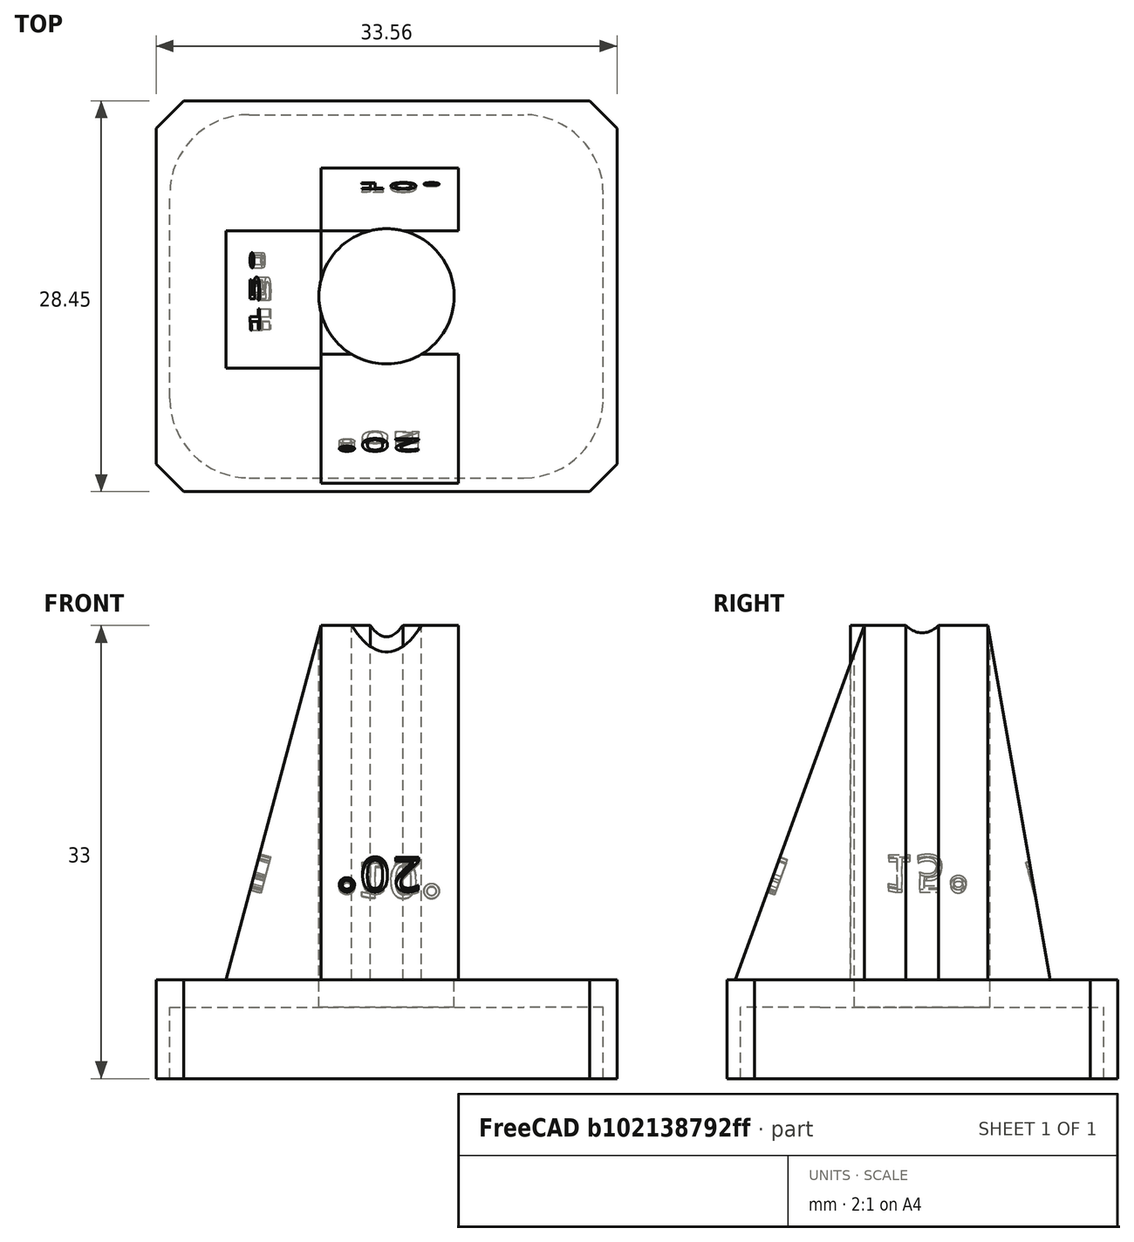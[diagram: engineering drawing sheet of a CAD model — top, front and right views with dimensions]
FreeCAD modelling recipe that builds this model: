
FCSTD DOCUMENT  (FreeCAD 0.19R24276 (Git))
Label: GuiaAfiladoTxeira
License: All rights reserved
LicenseURL: http://en.wikipedia.org/wiki/All_rights_reserved
objects: TechDraw::DrawViewDimension×12, TechDraw::DrawProjGroupItem×4, Part::Feature×3, Part::Box×2, Part::MultiFuse×2, TechDraw::DrawSVGTemplate×2, TechDraw::DrawViewPart×2, TechDraw::DrawPage×2, Part::Fillet×1, Part::Cylinder×1, Part::Offset×1, Part::Cut×1, Part::Chamfer×1, TechDraw::DrawProjGroup×1, TechDraw::DrawViewAnnotation×1
note: 12 computed .brp shape members not serialized (recipe doc carries the construction recipe); baked Part::Feature solids carry a one-line shape summary decoded from their .brp

FEATURE [Part::Box] Box  label="Cube"
  AttacherType = Attacher::AttachEngine3D
  Height = 5.2
  Length = 31.56
  Width = 26.45
FEATURE [Part::Fillet] Fillet
  Base = -> Box
  Edges = 4 edges r=5.78: [Edge1,Edge3,Edge5,Edge7]
FEATURE [Part::Box] Box001  label="Cube001"
  AttacherType = Attacher::AttachEngine3D
  Height = 7.2
  Length = 33.56
  Placement = pos=(-1,-1,0) rot=(0,0,1;0rad)
  Width = 28.45
FEATURE [Part::Cylinder] Cylinder
  Angle = 360
  AttacherType = Attacher::AttachEngine3D
  Height = 200
  Placement = pos=(15.78,13.22,0) rot=(0,0,1;0rad)
  Radius = 4.825
FEATURE [Part::Offset] Offset
  Fill = false
  Intersection = false
  Join = 0
  Mode = 0
  SelfIntersection = false
  Source = -> Cylinder
  Value = 0.1
FEATURE [Part::Feature] Part__Feature  label="Cut005"
  Placement = pos=(21,18,-5) rot=(0,-1,0;1.5708rad)
  shape: bbox 10 x 4.585 x 26 mm, 55 faces (baked)
FEATURE [Part::Feature] Part__Feature001  label="Cut006"
  Placement = pos=(11,9,-5) rot=(0.707107,0,0.707107;3.14159rad)
  shape: bbox 10 x 9.463 x 26 mm, 65 faces (baked)
FEATURE [Part::Feature] Part__Feature002  label="Cut001"
  Placement = pos=(11,18,-5) rot=(0.57735,-0.57735,0.57735;2.0944rad)
  shape: bbox 6.967 x 10 x 26 mm, 60 faces (baked)
FEATURE [Part::MultiFuse] Fusion
  Shapes = -> [Box001,Part__Feature,Part__Feature001,Part__Feature002]
FEATURE [Part::MultiFuse] Fusion001
  Shapes = -> [Offset,Fillet]
FEATURE [Part::Cut] Cut
  Base = -> Fusion
  Tool = -> Fusion001
FEATURE [Part::Chamfer] Chamfer
  Base = -> Cut
  Edges = 4 edges r=2: [Edge1,Edge3,Edge6,Edge24]
FEATURE [TechDraw::DrawSVGTemplate] Template
  EditableTexts = Designed_by_Name=<owner>; Drawing_number=001; FC-Date=-; FC-SC=1:1; FC-SH=1/2; FC-Title=KnifeSharpener; Subtitle=Afilador; Weight=<100gr
  Height = 210
  Orientation = 1
  Width = 297
FEATURE [TechDraw::DrawViewPart] View
  CoarseView = false
  Direction = (0.577,-0.577,0.577)
  Focus = 100
  HardHidden = false
  IsoCount = 0
  IsoHidden = false
  IsoVisible = false
  LockPosition = false
  Perspective = false
  Rotation = 0
  Scale = 2
  ScaleType = 0
  SeamHidden = false
  SeamVisible = true
  SmoothHidden = false
  SmoothVisible = true
  Source = -> [Chamfer]
  X = 215.123
  XDirection = (0.707,0.707,0)
  Y = 131.883
FEATURE [TechDraw::DrawSVGTemplate] Template001
  EditableTexts = Designed_by_Name=<owner>; Drawing_number=001; FC-Date=-; FC-SC=3:1; FC-SH=2/2; FC-Title=KnifeSharpener; Subtitle=Afilador; Weight=<100gr
  Height = 210
  Orientation = 1
  Width = 297
FEATURE [TechDraw::DrawViewPart] View001
  CoarseView = false
  Direction = (0.577,-0.577,0.577)
  Focus = 100
  HardHidden = false
  IsoCount = 0
  IsoHidden = false
  IsoVisible = false
  LockPosition = false
  Perspective = false
  Rotation = 0
  Scale = 3
  ScaleType = 0
  SeamHidden = false
  SeamVisible = true
  SmoothHidden = false
  SmoothVisible = true
  Source = -> [Chamfer]
  X = 143.3
  XDirection = (0.707,0.707,0)
  Y = 131
FEATURE [TechDraw::DrawProjGroupItem] ProjItem  label="Front"
  CoarseView = false
  Direction = (0,-1,0)
  Focus = 100
  HardHidden = false
  IsoCount = 0
  IsoHidden = false
  IsoVisible = false
  LockPosition = true
  Perspective = false
  Rotation = 0
  RotationVector = (1,0,0)
  ScaleType = 2
  SeamHidden = false
  SeamVisible = true
  SmoothHidden = false
  SmoothVisible = true
  Source = -> [Chamfer]
  Type = 0
  X = 0
  XDirection = (1,0,0)
  Y = 0
FEATURE [TechDraw::DrawProjGroupItem] ProjItem001  label="Right"
  CoarseView = false
  Direction = (1,-1e-16,0)
  Focus = 100
  HardHidden = false
  IsoCount = 0
  IsoHidden = false
  IsoVisible = false
  LockPosition = false
  Perspective = false
  Rotation = 0
  RotationVector = (1,0,0)
  ScaleType = 2
  SeamHidden = false
  SeamVisible = true
  SmoothHidden = false
  SmoothVisible = true
  Source = -> [Chamfer]
  Type = 2
  X = -46.005
  XDirection = (1e-16,1,0)
  Y = 0
FEATURE [TechDraw::DrawProjGroupItem] ProjItem002  label="Top"
  CoarseView = false
  Direction = (0,0,1)
  Focus = 100
  HardHidden = false
  IsoCount = 0
  IsoHidden = false
  IsoVisible = false
  LockPosition = false
  Perspective = false
  Rotation = 0
  RotationVector = (1,0,0)
  ScaleType = 2
  SeamHidden = false
  SeamVisible = true
  SmoothHidden = false
  SmoothVisible = true
  Source = -> [Chamfer]
  Type = 4
  X = 0
  XDirection = (1,0,0)
  Y = -50.275
FEATURE [TechDraw::DrawViewDimension] Dimension
  Arbitrary = false
  ArbitraryTolerances = false
  EqualTolerance = true
  FormatSpec = %.2f
  FormatSpecOverTolerance = %+.2f
  FormatSpecUnderTolerance = %+.2f
  Inverted = false
  LockPosition = false
  MeasureType = 1
  OverTolerance = 0
  References2D = -> [ProjItem002]
  Rotation = 0
  Scale = 2
  ScaleType = 0
  TheoreticalExact = false
  Type = 1
  UnderTolerance = 0
  X = -0.411648
  Y = -24.5744
FEATURE [TechDraw::DrawViewDimension] Dimension001
  Arbitrary = false
  ArbitraryTolerances = false
  EqualTolerance = true
  FormatSpec = %.2f
  FormatSpecOverTolerance = %+.2f
  FormatSpecUnderTolerance = %+.2f
  Inverted = false
  LockPosition = false
  MeasureType = 1
  OverTolerance = 0
  References2D = -> [ProjItem002]
  Rotation = 0
  Scale = 2
  ScaleType = 0
  TheoreticalExact = false
  Type = 2
  UnderTolerance = 0
  X = -39.0672
  Y = 3.49901
FEATURE [TechDraw::DrawViewDimension] Dimension002
  Arbitrary = false
  ArbitraryTolerances = false
  EqualTolerance = true
  FormatSpec = %.2f
  FormatSpecOverTolerance = %+.2f
  FormatSpecUnderTolerance = %+.2f
  Inverted = false
  LockPosition = false
  MeasureType = 1
  OverTolerance = 0
  References2D = -> [ProjItem]
  Rotation = 0
  Scale = 2
  ScaleType = 0
  TheoreticalExact = false
  Type = 2
  UnderTolerance = 0
  X = 29.6957
  Y = 2.5728
FEATURE [TechDraw::DrawViewDimension] Dimension003
  Arbitrary = false
  ArbitraryTolerances = false
  EqualTolerance = true
  FormatSpec = ⌀%.2f
  FormatSpecOverTolerance = %+.2f
  FormatSpecUnderTolerance = %+.2f
  Inverted = false
  LockPosition = false
  MeasureType = 1
  OverTolerance = 0
  References2D = -> [ProjItem002]
  Rotation = 0
  Scale = 2
  ScaleType = 0
  TheoreticalExact = false
  Type = 5
  UnderTolerance = 0
  X = 24.7681
  Y = 24.8205
FEATURE [TechDraw::DrawViewDimension] Dimension004
  Arbitrary = false
  ArbitraryTolerances = false
  EqualTolerance = true
  FormatSpec = %.2f
  FormatSpecOverTolerance = %+.2f
  FormatSpecUnderTolerance = %+.2f
  Inverted = false
  LockPosition = false
  MeasureType = 1
  OverTolerance = 0
  References2D = -> [View001]
  Rotation = 0
  Scale = 3
  ScaleType = 0
  TheoreticalExact = false
  Type = 0
  UnderTolerance = 0
  X = 24.7578
  Y = -35.6963
FEATURE [TechDraw::DrawViewDimension] Dimension005
  Arbitrary = false
  ArbitraryTolerances = false
  EqualTolerance = true
  FormatSpec = %.2f
  FormatSpecOverTolerance = %+.2f
  FormatSpecUnderTolerance = %+.2f
  Inverted = false
  LockPosition = false
  MeasureType = 1
  OverTolerance = 0
  References2D = -> [View001]
  Rotation = 0
  Scale = 3
  ScaleType = 0
  TheoreticalExact = false
  Type = 0
  UnderTolerance = 0
  X = -39.9824
  Y = -47.9058
FEATURE [TechDraw::DrawViewDimension] Dimension006
  Arbitrary = false
  ArbitraryTolerances = false
  EqualTolerance = true
  FormatSpec = %.2f
  FormatSpecOverTolerance = %+.2f
  FormatSpecUnderTolerance = %+.2f
  Inverted = false
  LockPosition = false
  MeasureType = 1
  OverTolerance = 0
  References2D = -> [View001]
  Rotation = 0
  Scale = 3
  ScaleType = 0
  TheoreticalExact = false
  Type = 0
  UnderTolerance = 0
  X = 32.2353
  Y = -17.3924
FEATURE [TechDraw::DrawViewDimension] Dimension007
  Arbitrary = false
  ArbitraryTolerances = false
  EqualTolerance = true
  FormatSpec = %.2f
  FormatSpecOverTolerance = %+.2f
  FormatSpecUnderTolerance = %+.2f
  Inverted = false
  LockPosition = false
  MeasureType = 1
  OverTolerance = 0
  References2D = -> [View001]
  Rotation = 0
  Scale = 3
  ScaleType = 0
  TheoreticalExact = false
  Type = 2
  UnderTolerance = 0
  X = 38.3646
  Y = 21.2792
FEATURE [TechDraw::DrawProjGroupItem] ProjItem003  label="Bottom"
  CoarseView = false
  Direction = (0,0,-1)
  Focus = 100
  HardHidden = false
  IsoCount = 0
  IsoHidden = false
  IsoVisible = false
  LockPosition = false
  Perspective = false
  Rotation = 0
  RotationVector = (1,0,0)
  ScaleType = 2
  SeamHidden = false
  SeamVisible = true
  SmoothHidden = false
  SmoothVisible = true
  Source = -> [Chamfer]
  Type = 5
  X = 0
  XDirection = (1,0,0)
  Y = 45.725
FEATURE [TechDraw::DrawProjGroup] ProjGroup
  Anchor = -> ProjItem
  AutoDistribute = true
  LockPosition = false
  ProjectionType = 0
  Rotation = 0
  ScaleType = 2
  Source = -> [Chamfer]
  Views = -> [ProjItem,ProjItem001,ProjItem002,ProjItem003]
  X = 102.874
  Y = 119.197
  spacingX = 15
  spacingY = 15
FEATURE [TechDraw::DrawViewDimension] Dimension008
  Arbitrary = false
  ArbitraryTolerances = false
  EqualTolerance = true
  FormatSpec = ⌀%.2f
  FormatSpecOverTolerance = %+.2f
  FormatSpecUnderTolerance = %+.2f
  Inverted = false
  LockPosition = false
  MeasureType = 1
  OverTolerance = 0
  References2D = -> [ProjItem003]
  Rotation = 0
  Scale = 2
  ScaleType = 0
  TheoreticalExact = false
  Type = 5
  UnderTolerance = 0
  X = -15.2946
  Y = 14.9608
FEATURE [TechDraw::DrawViewDimension] Dimension009
  Arbitrary = false
  ArbitraryTolerances = false
  EqualTolerance = true
  FormatSpec = %.2f
  FormatSpecOverTolerance = %+.2f
  FormatSpecUnderTolerance = %+.2f
  Inverted = false
  LockPosition = false
  MeasureType = 1
  OverTolerance = 0
  References2D = -> [ProjItem003]
  Rotation = 0
  Scale = 2
  ScaleType = 0
  TheoreticalExact = false
  Type = 1
  UnderTolerance = 0
  X = 28.3218
  Y = -14.8392
FEATURE [TechDraw::DrawViewDimension] Dimension010
  Arbitrary = false
  ArbitraryTolerances = false
  EqualTolerance = true
  FormatSpec = %.2f
  FormatSpecOverTolerance = %+.2f
  FormatSpecUnderTolerance = %+.2f
  Inverted = false
  LockPosition = false
  MeasureType = 1
  OverTolerance = 0
  References2D = -> [ProjItem003]
  Rotation = 0
  Scale = 2
  ScaleType = 0
  TheoreticalExact = false
  Type = 2
  UnderTolerance = 0
  X = 29.1338
  Y = 2.9349
FEATURE [TechDraw::DrawPage] Page  label="Vistas"
  KeepUpdated = true
  NextBalloonIndex = 1
  ProjectionType = 0
  Scale = 2
  Template = -> Template
  Views = -> [View,ProjGroup,Dimension,Dimension001,Dimension002,Dimension003,Dimension008,Dimension009,Dimension010]
FEATURE [TechDraw::DrawViewDimension] Dimension011
  Arbitrary = false
  ArbitraryTolerances = false
  EqualTolerance = true
  FormatSpec = %.2f
  FormatSpecOverTolerance = %+.2f
  FormatSpecUnderTolerance = %+.2f
  Inverted = false
  LockPosition = false
  MeasureType = 1
  OverTolerance = 0
  References2D = -> [View001]
  Rotation = 0
  Scale = 3
  ScaleType = 0
  TheoreticalExact = false
  Type = 0
  UnderTolerance = 0
  X = -54.3415
  Y = -9.92222
FEATURE [TechDraw::DrawViewAnnotation] Annotation
  Font = osifont
  LineSpace = 80
  LockPosition = false
  MaxWidth = -1
  Rotation = 0
  Scale = 3
  ScaleType = 0
  Text = Aproximate measurements: | Check with 3D piece
  TextSize = 5
  TextStyle = 0
  X = 54.2917
  Y = 61.6204
FEATURE [TechDraw::DrawPage] Page001  label="Cotas"
  KeepUpdated = true
  NextBalloonIndex = 1
  ProjectionType = 0
  Scale = 3
  Template = -> Template001
  Views = -> [View001,Dimension004,Dimension005,Dimension006,Dimension007,Dimension011,Annotation]
